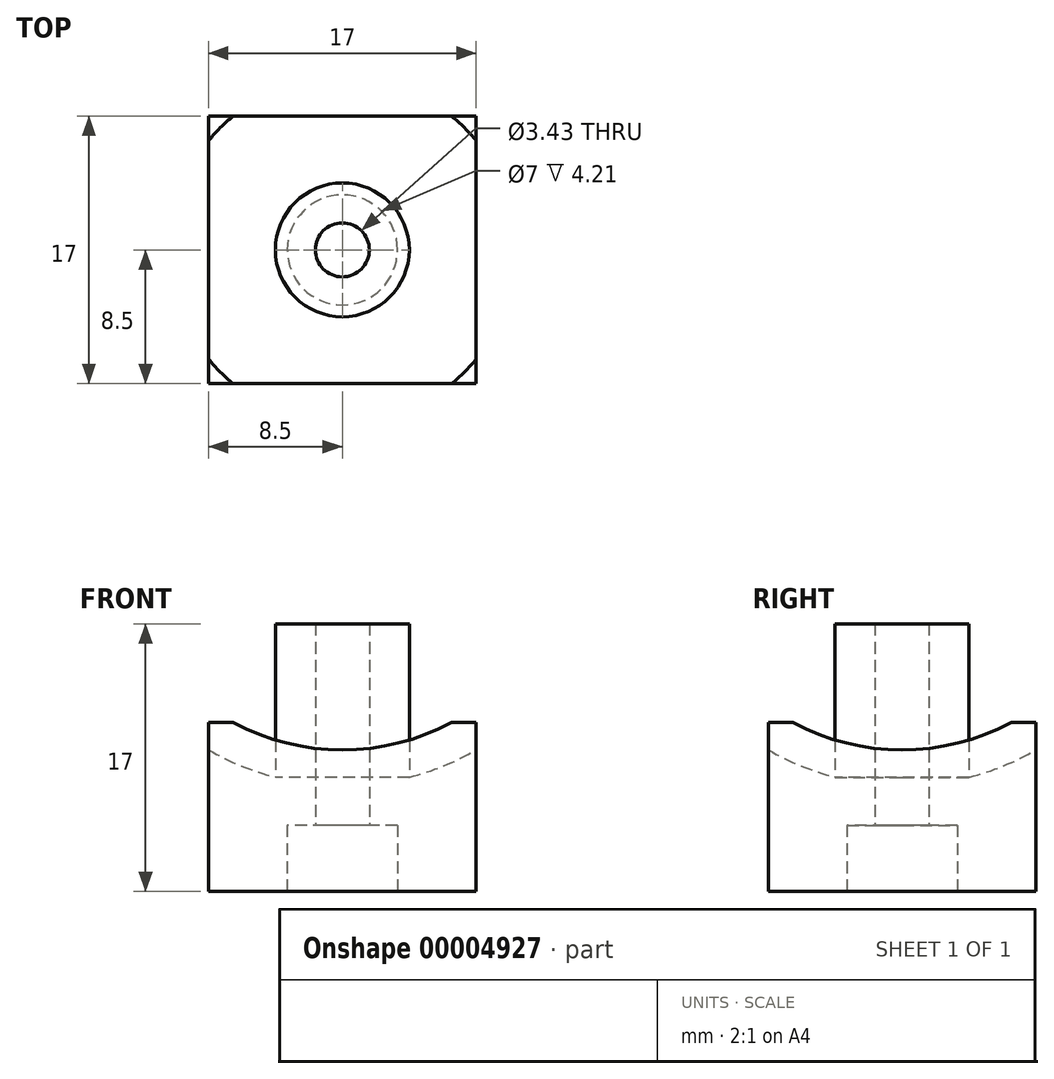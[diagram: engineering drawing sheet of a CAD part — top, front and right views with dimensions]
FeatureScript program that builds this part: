
annotation { "Feature Type Name" : "Feature", "Feature Type Description" : "" }
export const myFeature = defineFeature(function(context is Context, id is Id, definition is map)
    precondition{}
    {
        {
            var Q0;
            Q0=qCreatedBy(makeId("Front.planeOp"),FACE);
            var sketch = newSketch(context, id + "F0", { "sketchPlane" : qUnion([Q0])});
            skLineSegment(sketch, "E0", {"start": v(0, 0) * mm, "end": v(0, 25.5) * mm, "construction": true});
            skLineSegment(sketch, "E1.rect.bottom", {"start": v(25.5, 51) * mm, "end": v(-25.5, 51) * mm, "construction": true});
            skLineSegment(sketch, "E1.rect.top", {"start": v(25.5, 0) * mm, "end": v(-25.5, 0) * mm, "construction": true});
            skLineSegment(sketch, "E1.rect.left", {"start": v(25.5, 51) * mm, "end": v(25.5, 0) * mm, "construction": true});
            skLineSegment(sketch, "E1.rect.right", {"start": v(-25.5, 51) * mm, "end": v(-25.5, 0) * mm, "construction": true});
            skPoint(sketch, "E1.rect.middle", {"position": v(0, 25.5) * mm});
            skCircle(sketch, "E2", {"center": v(0, 25.5) * mm, "radius": 17.05 * mm, "construction": true});
            skLineSegment(sketch, "E3", {"start": v(0, 25.5) * mm, "end": v(0, 17) * mm, "construction": true});
            skLineSegment(sketch, "E4", {"start": v(-25.5, 0) * mm, "end": v(-8.5, 0) * mm, "construction": true});
            skLineSegment(sketch, "E5", {"start": v(0, 25.5) * mm, "end": v(-4.25, 25.5) * mm, "construction": true});
            skLineSegment(sketch, "E6", {"start": v(-4.25, 25.5) * mm, "end": v(-4.25, 21.25) * mm, "construction": true});
            skLineSegment(sketch, "E7", {"start": v(-4.25, 21.25) * mm, "end": v(0, 21.25) * mm, "construction": true});
            skLineSegment(sketch, "E8", {"start": v(-4.25, 21.25) * mm, "end": v(-4.25, 8.99) * mm, "construction": true});
            skLineSegment(sketch, "E9", {"start": v(-4.25, 8.99) * mm, "end": v(-16.51, 8.99) * mm, "construction": true});
            skLineSegment(sketch, "E10", {"start": v(-4.25, 21.25) * mm, "end": v(-16.51, 21.25) * mm, "construction": true});
            skLineSegment(sketch, "E11", {"start": v(-16.51, 21.25) * mm, "end": v(-16.51, 8.99) * mm, "construction": true});
            skLineSegment(sketch, "E12", {"start": v(-8.5, 0) * mm, "end": v(-8.5, 21.25) * mm, "construction": true});
            skLineSegment(sketch, "E13", {"start": v(-25.5, 0) * mm, "end": v(-25.5, 17) * mm, "construction": true});
            skLineSegment(sketch, "E14", {"start": v(-25.5, 17) * mm, "end": v(-4.25, 17) * mm, "construction": true});
            skLineSegment(sketch, "E15", {"start": v(-14.78, 8.99) * mm, "end": v(-14.78, 21.25) * mm, "construction": true});
            skPoint(sketch, "E16", {"position": v(-14.78, 17) * mm});
            skPoint(sketch, "E17", {"position": v(-8.5, 10.72) * mm});
            skLineSegment(sketch, "E18", {"start": v(-4.25, 10.72) * mm, "end": v(-16.51, 10.72) * mm, "construction": true});
            skSolve(sketch);
        }
        {
            var Q0;
            Q0=qCreatedBy(makeId("Front.planeOp"),FACE);
            var sketch = newSketch(context, id + "F1", { "sketchPlane" : qUnion([Q0])});
            skLineSegment(sketch, "E19.bottom", {"start": v(-8.5, 10.72) * mm, "end": v(8.5, 10.72) * mm});
            skLineSegment(sketch, "E19.top", {"start": v(-8.5, 0) * mm, "end": v(8.5, 0) * mm});
            skLineSegment(sketch, "E19.left", {"start": v(-8.5, 10.72) * mm, "end": v(-8.5, 0) * mm});
            skLineSegment(sketch, "E19.right", {"start": v(8.5, 10.72) * mm, "end": v(8.5, 0) * mm});
            skPoint(sketch, "E20", {"position": v(-8.5, 8.99) * mm});
            skSolve(sketch);
        }
        {
            var Q0;
            Q0=qCreatedBy(makeId("Front.planeOp"),FACE);
            var sketch = newSketch(context, id + "F2", { "sketchPlane" : qUnion([Q0])});
            skArc(sketch, "E21", {"start": v(-17, 23.71) * mm, "mid": v(0, 6.71) * mm, "end": v(17, 23.71) * mm});
            skLineSegment(sketch, "E22", {"start": v(-17, 23.71) * mm, "end": v(17, 23.71) * mm});
            skLineSegment(sketch, "E23", {"start": v(0, 6.71) * mm, "end": v(0, 10.72) * mm, "construction": true});
            skSolve(sketch);
        }
        {
            var Q0;
            Q0 = qSketchRegion(id + "F1", true);
            extrude(context, id + "F3", {"entities" : qUnion([Q0]), "endBound" : BoundingType.SYMMETRIC, "depth" : 17 * mm});
        }
        {
            var Q0;
            Q0=makeQuery(id+"F2.imprint","IMPRINT",FACE,{"disambiguationData":[TD([[makeQuery(id+"F2.imprint","IMPRINT",EDGE,{"derivedFrom":sQuery(id+"F2.wireOp",EDGE,"E21")}),1.0]])]});
            var Q1;
            Q1=sQuery(id+"F2.wireOp",EDGE,"E22");
            revolve(context, id + "F4", {"operationType" : NewBodyOperationType.REMOVE, "entities" : qUnion([Q0]), "axis" : qUnion([Q1]), "revolveType" : RevolveType.FULL, "oppositeDirection" : true});
        }
        {
            var Q0;
            Q0=qCreatedBy(makeId("Top.planeOp"),FACE);
            var sketch = newSketch(context, id + "F5", { "sketchPlane" : qUnion([Q0])});
            skCircle(sketch, "E24", {"center": v(0, 0) * mm, "radius": 1.71 * mm});
            skCircle(sketch, "E25.0", {"center": v(0, 0) * mm, "radius": 4.25 * mm});
            skSolve(sketch);
        }
        {
            var Q0;
            Q0=qCreatedBy(makeId("Top.planeOp"),FACE);
            var sketch = newSketch(context, id + "F6", { "sketchPlane" : qUnion([Q0])});
            skCircle(sketch, "E26", {"center": v(0, 0) * mm, "radius": 3.5 * mm});
            skCircle(sketch, "E27.0", {"center": v(0, 0) * mm, "radius": 6 * mm});
            skSolve(sketch);
        }
        {
            var Q0;
            Q0=makeQuery(id+"F5.imprint","IMPRINT",FACE,{"disambiguationData":[TD([[makeQuery(id+"F5.imprint","IMPRINT",EDGE,{"derivedFrom":sQuery(id+"F5.wireOp",EDGE,"E24")}),-1.0]])]});
            extrude(context, id + "F7", {"entities" : qUnion([Q0]), "operationType" : NewBodyOperationType.ADD, "depth" : 17 * mm});
        }
        {
            var Q0;
            Q0=makeQuery(id+"F6.imprint","IMPRINT",FACE,{"disambiguationData":[TD([[makeQuery(id+"F6.imprint","IMPRINT",EDGE,{"derivedFrom":sQuery(id+"F6.wireOp",EDGE,"E26")}),1.0]])]});
            extrude(context, id + "F8", {"entities" : qUnion([Q0]), "operationType" : NewBodyOperationType.REMOVE, "depth" : 4.2 * mm});
        }
        {
            var Q0;
            Q0=makeQuery(id+"F5.imprint","IMPRINT",FACE,{"disambiguationData":[TD([[makeQuery(id+"F5.imprint","IMPRINT",EDGE,{"derivedFrom":sQuery(id+"F5.wireOp",EDGE,"E24")}),1.0]])]});
            extrude(context, id + "F9", {"entities" : qUnion([Q0]), "operationType" : NewBodyOperationType.REMOVE, "depth" : 17 * mm});
        }
    });
